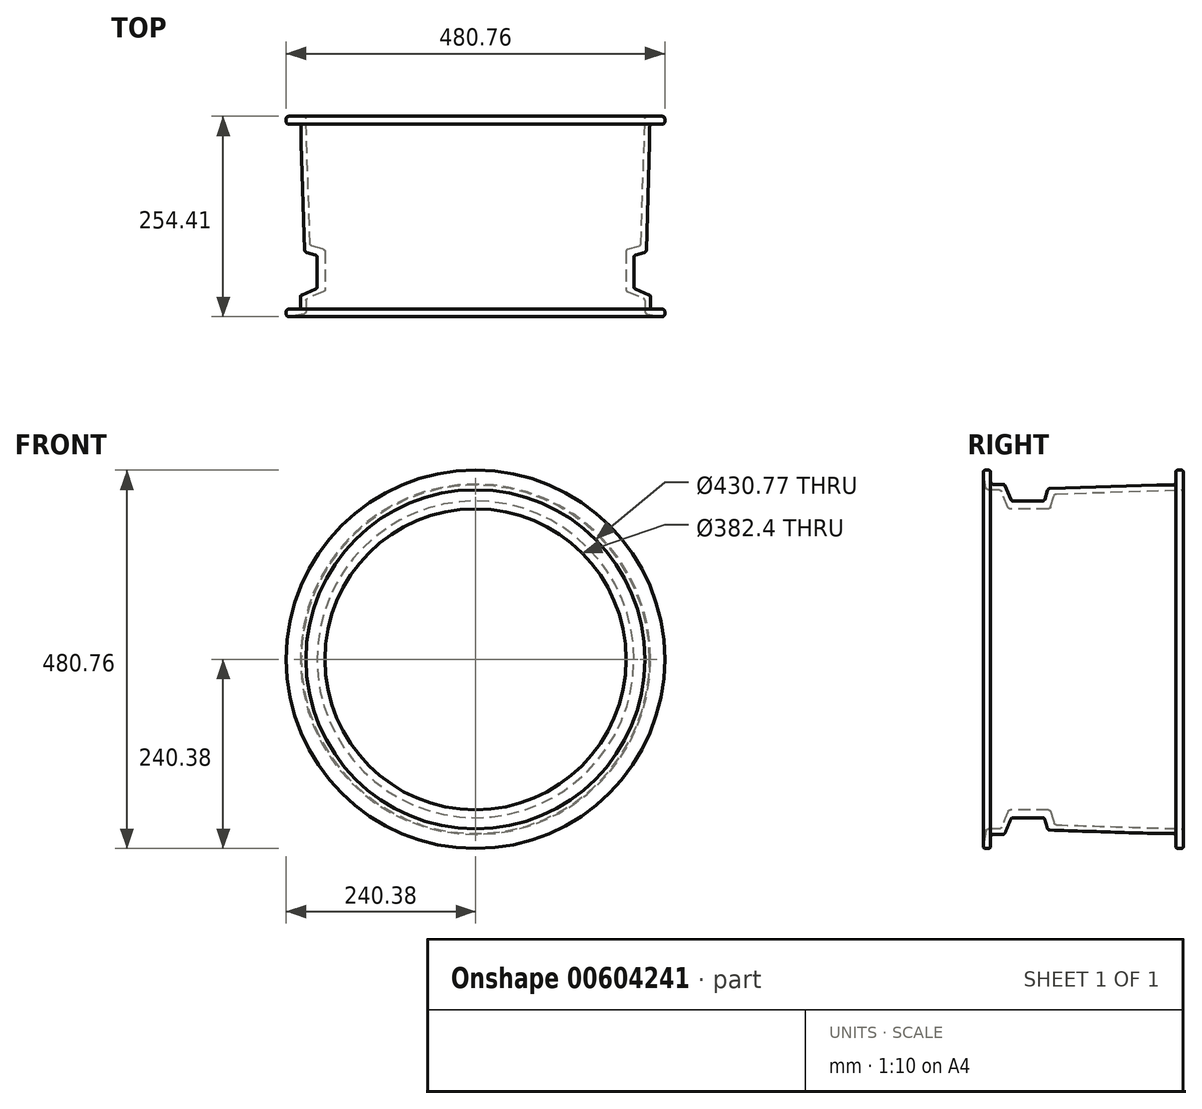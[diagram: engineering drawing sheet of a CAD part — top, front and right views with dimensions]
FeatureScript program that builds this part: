
annotation { "Feature Type Name" : "Feature", "Feature Type Description" : "" }
export const myFeature = defineFeature(function(context is Context, id is Id, definition is map)
    precondition{}
    {
        {
            var Q0;
            Q0=qCreatedBy(makeId("Right.planeOp"),FACE);
            var sketch = newSketch(context, id + "F0", { "sketchPlane" : qUnion([Q0])});
            skLineSegment(sketch, "E0", {"start": v(-126.72, 240.38) * mm, "end": v(-123.3, 240.38) * mm});
            skLineSegment(sketch, "E1", {"start": v(-120.3, 237.38) * mm, "end": v(-120.3, 225.38) * mm});
            skLineSegment(sketch, "E2", {"start": v(-117.3, 222.38) * mm, "end": v(-104.84, 222.38) * mm});
            skLineSegment(sketch, "E3", {"start": v(-102.07, 220.54) * mm, "end": v(-94.74, 203.04) * mm});
            skLineSegment(sketch, "E4", {"start": v(-91.97, 201.2) * mm, "end": v(-54.45, 201.2) * mm});
            skLineSegment(sketch, "E5", {"start": v(-51.57, 203.33) * mm, "end": v(-48.1, 214.8) * mm});
            skLineSegment(sketch, "E6", {"start": v(-45.32, 216.94) * mm, "end": v(90.77, 221.3) * mm});
            skLineSegment(sketch, "E7", {"start": v(90.86, 221.3) * mm, "end": v(111.7, 221.3) * mm});
            skLineSegment(sketch, "E8", {"start": v(114.7, 224.3) * mm, "end": v(114.7, 237.38) * mm});
            skLineSegment(sketch, "E9", {"start": v(117.7, 240.38) * mm, "end": v(121.7, 240.38) * mm});
            skLineSegment(sketch, "E10", {"start": v(124.7, 237.38) * mm, "end": v(124.7, 218.29) * mm});
            skLineSegment(sketch, "E11", {"start": v(121.79, 215.3) * mm, "end": v(-36.91, 210.2) * mm});
            skLineSegment(sketch, "E12", {"start": v(-39.69, 208.07) * mm, "end": v(-44.16, 193.33) * mm});
            skLineSegment(sketch, "E13", {"start": v(-47.03, 191.2) * mm, "end": v(-95.38, 191.2) * mm});
            skLineSegment(sketch, "E14", {"start": v(-98.14, 193.04) * mm, "end": v(-106.73, 213.54) * mm});
            skLineSegment(sketch, "E15", {"start": v(-109.5, 215.38) * mm, "end": v(-123.3, 215.38) * mm});
            skLineSegment(sketch, "E16", {"start": v(-126.26, 217.85) * mm, "end": v(-129.67, 236.85) * mm});
            skPoint(sketch, "E17.visualSharp", {"position": v(-120.3, 222.38) * mm});
            skArc(sketch, "E17.filletArc", {"start": v(-120.3, 225.38) * mm, "mid": v(-119.43, 223.26) * mm, "end": v(-117.3, 222.38) * mm});
            skPoint(sketch, "E18.visualSharp", {"position": v(-102.84, 222.38) * mm});
            skArc(sketch, "E18.filletArc", {"start": v(-102.07, 220.54) * mm, "mid": v(-103.17, 221.88) * mm, "end": v(-104.84, 222.38) * mm});
            skPoint(sketch, "E19.visualSharp", {"position": v(-93.97, 201.2) * mm});
            skArc(sketch, "E19.filletArc", {"start": v(-94.74, 203.04) * mm, "mid": v(-93.64, 201.7) * mm, "end": v(-91.97, 201.2) * mm});
            skPoint(sketch, "E20.visualSharp", {"position": v(-52.22, 201.2) * mm});
            skArc(sketch, "E20.filletArc", {"start": v(-54.45, 201.2) * mm, "mid": v(-52.66, 201.8) * mm, "end": v(-51.57, 203.33) * mm});
            skPoint(sketch, "E21.visualSharp", {"position": v(-47.47, 216.87) * mm});
            skArc(sketch, "E21.filletArc", {"start": v(-45.32, 216.94) * mm, "mid": v(-47.05, 216.32) * mm, "end": v(-48.1, 214.8) * mm});
            skPoint(sketch, "E22.visualSharp", {"position": v(114.7, 221.3) * mm});
            skArc(sketch, "E22.filletArc", {"start": v(111.7, 221.3) * mm, "mid": v(113.81, 222.18) * mm, "end": v(114.7, 224.3) * mm});
            skPoint(sketch, "E23.visualSharp", {"position": v(90.82, 221.3) * mm});
            skArc(sketch, "E23.filletArc", {"start": v(90.86, 221.3) * mm, "mid": v(90.82, 221.3) * mm, "end": v(90.77, 221.3) * mm});
            skPoint(sketch, "E24.visualSharp", {"position": v(-125.82, 215.38) * mm});
            skArc(sketch, "E24.filletArc", {"start": v(-126.26, 217.85) * mm, "mid": v(-125.23, 216.08) * mm, "end": v(-123.3, 215.38) * mm});
            skPoint(sketch, "E25.visualSharp", {"position": v(-130.3, 240.38) * mm});
            skArc(sketch, "E25.filletArc", {"start": v(-126.72, 240.38) * mm, "mid": v(-129.02, 239.3) * mm, "end": v(-129.67, 236.85) * mm});
            skPoint(sketch, "E26.visualSharp", {"position": v(-120.3, 240.38) * mm});
            skArc(sketch, "E26.filletArc", {"start": v(-120.3, 237.38) * mm, "mid": v(-121.19, 239.5) * mm, "end": v(-123.3, 240.38) * mm});
            skPoint(sketch, "E27.visualSharp", {"position": v(-39.06, 210.13) * mm});
            skArc(sketch, "E27.filletArc", {"start": v(-36.91, 210.2) * mm, "mid": v(-38.64, 209.58) * mm, "end": v(-39.69, 208.07) * mm});
            skPoint(sketch, "E28.visualSharp", {"position": v(124.7, 215.38) * mm});
            skArc(sketch, "E28.filletArc", {"start": v(121.79, 215.3) * mm, "mid": v(123.85, 216.2) * mm, "end": v(124.7, 218.29) * mm});
            skPoint(sketch, "E29.visualSharp", {"position": v(124.7, 240.38) * mm});
            skArc(sketch, "E29.filletArc", {"start": v(124.7, 237.38) * mm, "mid": v(123.81, 239.5) * mm, "end": v(121.7, 240.38) * mm});
            skPoint(sketch, "E30.visualSharp", {"position": v(114.7, 240.38) * mm});
            skArc(sketch, "E30.filletArc", {"start": v(117.7, 240.38) * mm, "mid": v(115.57, 239.5) * mm, "end": v(114.7, 237.38) * mm});
            skPoint(sketch, "E31.visualSharp", {"position": v(-97.37, 191.2) * mm});
            skArc(sketch, "E31.filletArc", {"start": v(-98.14, 193.04) * mm, "mid": v(-97.04, 191.7) * mm, "end": v(-95.38, 191.2) * mm});
            skPoint(sketch, "E32.visualSharp", {"position": v(-44.8, 191.2) * mm});
            skArc(sketch, "E32.filletArc", {"start": v(-47.03, 191.2) * mm, "mid": v(-45.24, 191.8) * mm, "end": v(-44.16, 193.33) * mm});
            skPoint(sketch, "E33.visualSharp", {"position": v(-107.5, 215.38) * mm});
            skArc(sketch, "E33.filletArc", {"start": v(-106.73, 213.54) * mm, "mid": v(-107.83, 214.88) * mm, "end": v(-109.5, 215.38) * mm});
            skLineSegment(sketch, "E34", {"start": v(-74.78, 0) * mm, "end": v(0, 0) * mm});
            skSolve(sketch);
        }
        {
            var Q0;
            Q0 = qSketchRegion(id + "F0", true);
            var Q1;
            Q1=sQuery(id+"F0.wireOp",EDGE,"E34");
            revolve(context, id + "F1", {"entities" : qUnion([Q0]), "axis" : qUnion([Q1]), "revolveType" : RevolveType.FULL});
        }
    });
